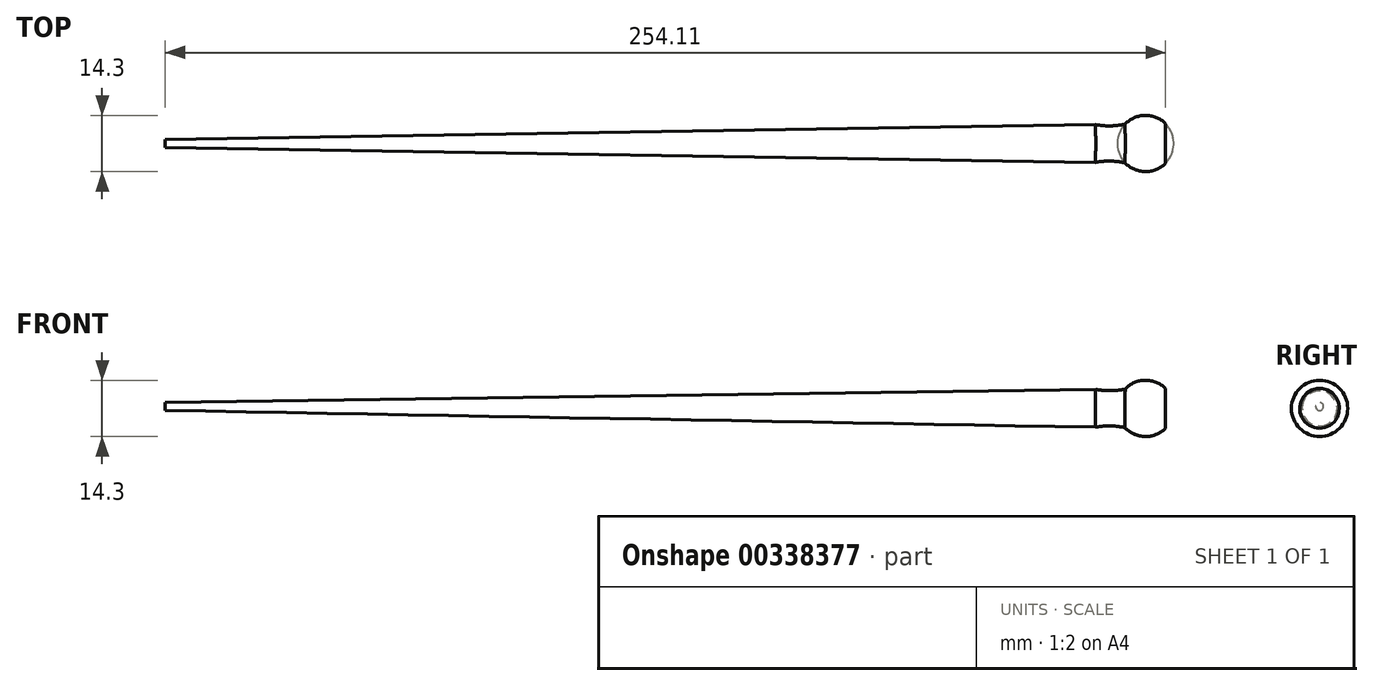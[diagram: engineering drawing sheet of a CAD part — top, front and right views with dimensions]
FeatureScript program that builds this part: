
annotation { "Feature Type Name" : "Feature", "Feature Type Description" : "" }
export const myFeature = defineFeature(function(context is Context, id is Id, definition is map)
    precondition{}
    {
        {
            var Q0;
            Q0=qCreatedBy(makeId("Front.planeOp"),FACE);
            var sketch = newSketch(context, id + "F0", { "sketchPlane" : qUnion([Q0])});
            skLineSegment(sketch, "E0.bottom", {"start": v(0, 0) * mm, "end": v(-254, 0.5) * mm});
            skLineSegment(sketch, "E0.left", {"start": v(0, 0) * mm, "end": v(0, -5.08) * mm});
            skLineSegment(sketch, "E0.right", {"start": v(-254, 0.5) * mm, "end": v(-254, -0.5) * mm});
            skLineSegment(sketch, "E1", {"start": v(0, 0) * mm, "end": v(12.7, 0) * mm});
            skLineSegment(sketch, "E2", {"start": v(10.39, 0) * mm, "end": v(10.39, -6.8) * mm});
            skArc(sketch, "E3", {"start": v(10.39, -6.8) * mm, "mid": v(11.95, -3.54) * mm, "end": v(12.7, 0) * mm});
            skArc(sketch, "E4", {"start": v(10.39, -6.8) * mm, "mid": v(5.32, -5.14) * mm, "end": v(0, -5.08) * mm});
            skLineSegment(sketch, "E5", {"start": v(0, -5.08) * mm, "end": v(-254, -0.5) * mm});
            skArc(sketch, "E6", {"start": v(-12.1, 0.02) * mm, "mid": v(-4.96, -7.14) * mm, "end": v(2.2, 0) * mm});
            skArc(sketch, "E7", {"start": v(-10.15, -4.9) * mm, "mid": v(-13.9, -4.45) * mm, "end": v(-17.65, -4.76) * mm});
            skSolve(sketch);
        }
        {
            var Q0;
            {var subQ5=sQuery(id+"F0.wireOp",EDGE,"E0.right");Q0=makeQuery(id+"F0.imprint","IMPRINT",FACE,{"disambiguationData":[TD([[makeQuery(id+"F0.imprint","IMPRINT",EDGE,{"derivedFrom":subQ5}),1.0]])]});}
            var Q1;
            {var subQ1=sQuery(id+"F0.wireOp",EDGE,"E4");var subQ3=sQuery(id+"F0.wireOp",EDGE,"E6");var subQ4=makeQuery(id+"F0.imprint","INTERSECT",VERTEX,{"derivedFrom":[subQ1,subQ3]});Q1=makeQuery(id+"F0.imprint","IMPRINT",FACE,{"disambiguationData":[TD([[makeQuery(id+"F0.imprint","IMPRINT",EDGE,{"disambiguationData":[TD([[subQ4,-1.0]])],"derivedFrom":subQ1}),1.0]])]});}
            var Q2;
            {var subQ0=sQuery(id+"F0.wireOp",EDGE,"E0.left");Q2=makeQuery(id+"F0.imprint","IMPRINT",FACE,{"disambiguationData":[TD([[makeQuery(id+"F0.imprint","IMPRINT",EDGE,{"derivedFrom":subQ0}),-1.0]])]});}
            var Q3;
            Q3=sQuery(id+"F0.wireOp",EDGE,"E0.bottom");
            revolve(context, id + "F1", {"entities" : qUnion([Q0, Q1, Q2]), "axis" : qUnion([Q3]), "revolveType" : RevolveType.FULL});
        }
    });
